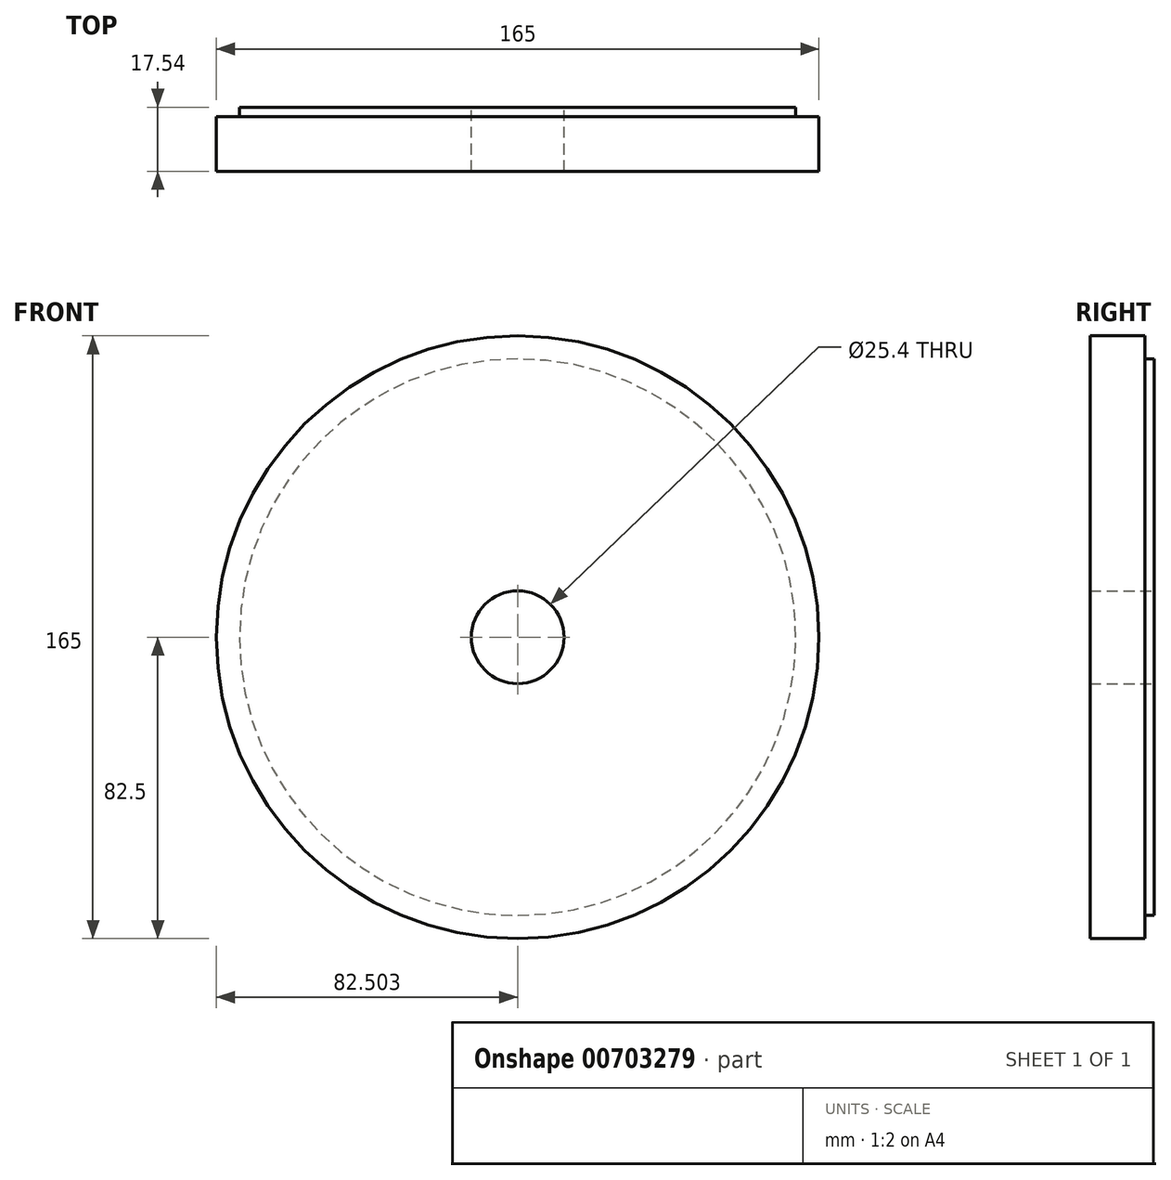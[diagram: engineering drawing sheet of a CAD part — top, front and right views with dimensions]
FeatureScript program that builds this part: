
annotation { "Feature Type Name" : "Feature", "Feature Type Description" : "" }
export const myFeature = defineFeature(function(context is Context, id is Id, definition is map)
    precondition{}
    {
        {
            var Q0;
            Q0=qCreatedBy(makeId("Top.planeOp"),FACE);
            var sketch = newSketch(context, id + "F0", { "sketchPlane" : qUnion([Q0])});
            skLineSegment(sketch, "E0.bottom", {"start": v(-17.22, -41.12) * mm, "end": v(65.28, -41.12) * mm});
            skLineSegment(sketch, "E0.top", {"start": v(-17.22, -56.12) * mm, "end": v(65.28, -56.12) * mm});
            skLineSegment(sketch, "E0.left", {"start": v(-17.22, -41.12) * mm, "end": v(-17.22, -56.12) * mm});
            skLineSegment(sketch, "E0.right", {"start": v(65.28, -41.12) * mm, "end": v(65.28, -56.12) * mm});
            skLineSegment(sketch, "E1.bottom", {"start": v(65.28, -41.12) * mm, "end": v(52.58, -41.12) * mm});
            skLineSegment(sketch, "E2.top", {"start": v(-10.87, -38.58) * mm, "end": v(52.58, -38.58) * mm});
            skLineSegment(sketch, "E3", {"start": v(52.58, -38.58) * mm, "end": v(52.58, -41.12) * mm});
            skLineSegment(sketch, "E4", {"start": v(-10.87, -38.58) * mm, "end": v(-10.87, -41.12) * mm});
            skLineSegment(sketch, "E5", {"start": v(52.58, -41.12) * mm, "end": v(52.58, -56.12) * mm});
            skSolve(sketch);
        }
        {
            var Q0;
            {var subQ0=sQuery(id+"F0.wireOp",EDGE,"E0.left");Q0=makeQuery(id+"F0.imprint","IMPRINT",FACE,{"disambiguationData":[TD([[makeQuery(id+"F0.imprint","IMPRINT",EDGE,{"derivedFrom":subQ0}),1.0]])]});}
            var Q1;
            Q1=makeQuery(id+"F0.imprint","IMPRINT",FACE,{"disambiguationData":[TD([[makeQuery(id+"F0.imprint","IMPRINT",EDGE,{"derivedFrom":sQuery(id+"F0.wireOp",EDGE,"E1.bottom")}),-1.0]])]});
            var Q2;
            Q2=makeQuery(id+"F0.imprint","IMPRINT",FACE,{"disambiguationData":[TD([[makeQuery(id+"F0.imprint","IMPRINT",EDGE,{"derivedFrom":sQuery(id+"F0.wireOp",EDGE,"L3yjhRYw-GHsK-NQlI-CaUR-nhx9vXlwbOS5.bottom")}),-1.0]])]});
            var Q3;
            Q3=makeQuery(id+"F0.imprint","IMPRINT",FACE,{"disambiguationData":[TD([[makeQuery(id+"F0.imprint","IMPRINT",EDGE,{"derivedFrom":sQuery(id+"F0.wireOp",EDGE,"E2.bottom")}),1.0]])]});
            var Q4;
            Q4=makeQuery(id+"F0.imprint","IMPRINT",FACE,{"disambiguationData":[TD([[makeQuery(id+"F0.imprint","IMPRINT",EDGE,{"derivedFrom":sQuery(id+"F0.wireOp",EDGE,"E2.top")}),-1.0]])]});
            var Q5;
            Q5=sQuery(id+"F0.wireOp",EDGE,"E0.right");
            revolve(context, id + "F1", {"surfaceOperationType" : NewSurfaceOperationType.NEW, "entities" : qUnion([Q0, Q1, Q2, Q3, Q4]), "axis" : qUnion([Q5]), "revolveType" : RevolveType.FULL});
        }
    });
